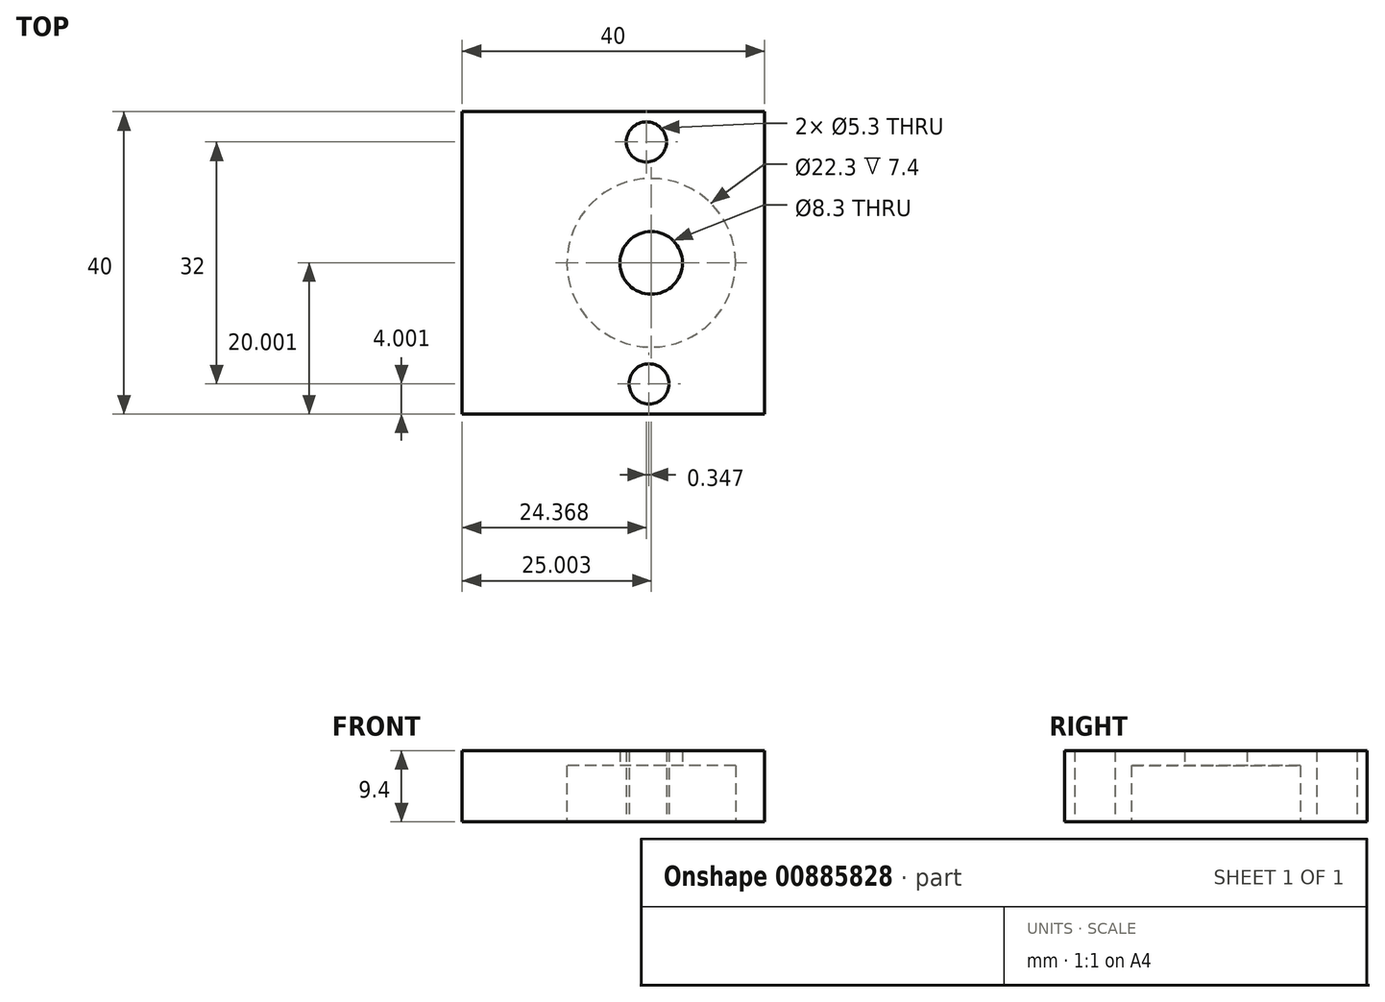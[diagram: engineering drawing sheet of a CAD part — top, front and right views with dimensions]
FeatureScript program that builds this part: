
annotation { "Feature Type Name" : "Feature", "Feature Type Description" : "" }
export const myFeature = defineFeature(function(context is Context, id is Id, definition is map)
    precondition{}
    {
        {
            var Q0;
            Q0=qCreatedBy(makeId("Top.planeOp"),FACE);
            var sketch = newSketch(context, id + "F0", { "sketchPlane" : qUnion([Q0])});
            skLineSegment(sketch, "E0.bottom", {"start": v(-86.26, -17.28) * mm, "end": v(-66.26, -17.28) * mm});
            skLineSegment(sketch, "E0.top", {"start": v(-86.26, -57.28) * mm, "end": v(-66.26, -57.28) * mm});
            skLineSegment(sketch, "E0.left", {"start": v(-86.26, -17.28) * mm, "end": v(-86.26, -57.28) * mm});
            skLineSegment(sketch, "E0.right", {"start": v(-66.26, -17.28) * mm, "end": v(-66.26, -57.28) * mm});
            skCircle(sketch, "E1", {"center": v(-76.26, -24.28) * mm, "radius": 2.65 * mm});
            skCircle(sketch, "E2", {"center": v(-76.26, -37.28) * mm, "radius": 2.65 * mm});
            skCircle(sketch, "E3", {"center": v(-76.26, -50.28) * mm, "radius": 2.65 * mm});
            skPoint(sketch, "E4", {"position": v(-66.26, -17.28) * mm});
            skPoint(sketch, "E5", {"position": v(-66.26, -57.28) * mm});
            skLineSegment(sketch, "E6.bottom", {"start": v(-66.26, -17.28) * mm, "end": v(-26.26, -17.28) * mm});
            skLineSegment(sketch, "E6.top", {"start": v(-66.26, -57.28) * mm, "end": v(-26.26, -57.28) * mm});
            skLineSegment(sketch, "E6.right", {"start": v(-26.26, -17.28) * mm, "end": v(-26.26, -57.28) * mm});
            skCircle(sketch, "E7", {"center": v(-41.26, -37.28) * mm, "radius": 4.15 * mm});
            skCircle(sketch, "E8", {"center": v(-41.26, -37.28) * mm, "radius": 11.15 * mm});
            skCircle(sketch, "E9", {"center": v(-41.9, -21.28) * mm, "radius": 2.65 * mm});
            skCircle(sketch, "E10", {"center": v(-41.54, -53.28) * mm, "radius": 2.65 * mm});
            skSolve(sketch);
        }
        {
            var Q0;
            Q0=makeQuery(id+"F0.imprint","IMPRINT",FACE,{"disambiguationData":[TD([[makeQuery(id+"F0.imprint","IMPRINT",EDGE,{"derivedFrom":sQuery(id+"F0.wireOp",EDGE,"E6.bottom")}),-1.0]])]});
            extrude(context, id + "F1", {"entities" : qUnion([Q0]), "depth" : 7.4 * mm});
        }
        {
            var Q0;
            Q0=makeQuery(id+"F1.opExtrude","CAP_FACE",FACE,{"disambiguationData":[OSD([sQuery(id+"F0.wireOp",EDGE,"E6.bottom"),sQuery(id+"F0.wireOp",EDGE,"E6.top"),sQuery(id+"F0.wireOp",EDGE,"E0.right"),sQuery(id+"F0.wireOp",EDGE,"E6.right"),sQuery(id+"F0.wireOp",EDGE,"E8"),sQuery(id+"F0.wireOp",EDGE,"E9"),sQuery(id+"F0.wireOp",EDGE,"E10")])],"isStart":false});
            var sketch = newSketch(context, id + "F2", { "sketchPlane" : qUnion([Q0])});
            skLineSegment(sketch, "E11.bottom", {"start": v(-66.26, -17.28) * mm, "end": v(-26.26, -17.28) * mm});
            skLineSegment(sketch, "E11.top", {"start": v(-66.26, -57.28) * mm, "end": v(-26.26, -57.28) * mm});
            skLineSegment(sketch, "E11.left", {"start": v(-66.26, -17.28) * mm, "end": v(-66.26, -57.28) * mm});
            skLineSegment(sketch, "E11.right", {"start": v(-26.26, -17.28) * mm, "end": v(-26.26, -57.28) * mm});
            skSolve(sketch);
        }
        {
            var Q0;
            Q0=makeQuery(id+"F2.imprint","IMPRINT",FACE,{"disambiguationData":[TD([[makeQuery(id+"F2.imprint","IMPRINT",EDGE,{"derivedFrom":sQuery(id+"F2.wireOp",EDGE,"E11.bottom")}),-1.0]])]});
            var sketch = newSketch(context, id + "F3", { "sketchPlane" : qUnion([Q0])});
            skLineSegment(sketch, "E12.bottom", {"start": v(-66.26, -17.28) * mm, "end": v(-26.26, -17.28) * mm});
            skLineSegment(sketch, "E12.top", {"start": v(-66.26, -57.28) * mm, "end": v(-26.26, -57.28) * mm});
            skLineSegment(sketch, "E12.left", {"start": v(-66.26, -17.28) * mm, "end": v(-66.26, -57.28) * mm});
            skLineSegment(sketch, "E12.right", {"start": v(-26.26, -17.28) * mm, "end": v(-26.26, -57.28) * mm});
            skPoint(sketch, "E13", {"position": v(-26.26, -17.28) * mm});
            skSolve(sketch);
        }
        {
            var Q0;
            Q0=qSketchRegion(id+"F3",true);
            var Q1;
            Q1=makeQuery(id+"F2.imprint","IMPRINT",FACE,{"disambiguationData":[TD([[makeQuery(id+"F2.imprint","IMPRINT",EDGE,{"derivedFrom":sQuery(id+"F2.wireOp",EDGE,"E11.bottom")}),-1.0]])]});
            extrude(context, id + "F4", {"entities" : qUnion([Q0, Q1]), "operationType" : NewBodyOperationType.ADD, "depth" : 2 * mm});
        }
        {
            var Q0;
            Q0=makeQuery(id+"F4.boolean.opBoolean","MERGE",FACE,{"disambiguationData":[OD(1.0)],"derivedFrom":[makeQuery(id+"F4.opExtrude","CAP_FACE",FACE,{"disambiguationData":[OSD([sQuery(id+"F0.wireOp",EDGE,"E8"),sQuery(id+"F0.wireOp",EDGE,"E9"),sQuery(id+"F0.wireOp",EDGE,"E10"),sQuery(id+"F2.wireOp",EDGE,"E11.bottom"),sQuery(id+"F2.wireOp",EDGE,"E11.top"),sQuery(id+"F2.wireOp",EDGE,"E11.left"),sQuery(id+"F2.wireOp",EDGE,"E11.right")])],"isStart":true}),makeQuery(id+"F4.opExtrude","CAP_FACE",FACE,{"disambiguationData":[OSD([sQuery(id+"F3.wireOp",EDGE,"E12.bottom"),sQuery(id+"F3.wireOp",EDGE,"E12.top"),sQuery(id+"F3.wireOp",EDGE,"E12.left"),sQuery(id+"F3.wireOp",EDGE,"E12.right")])],"isStart":true})]});
            var Q1;
            Q1=makeQuery(id+"F4.boolean.opBoolean","MERGE",FACE,{"disambiguationData":[OD(2.0)],"derivedFrom":[makeQuery(id+"F4.opExtrude","CAP_FACE",FACE,{"disambiguationData":[OSD([sQuery(id+"F0.wireOp",EDGE,"E8"),sQuery(id+"F0.wireOp",EDGE,"E9"),sQuery(id+"F0.wireOp",EDGE,"E10"),sQuery(id+"F2.wireOp",EDGE,"E11.bottom"),sQuery(id+"F2.wireOp",EDGE,"E11.top"),sQuery(id+"F2.wireOp",EDGE,"E11.left"),sQuery(id+"F2.wireOp",EDGE,"E11.right")])],"isStart":true}),makeQuery(id+"F4.opExtrude","CAP_FACE",FACE,{"disambiguationData":[OSD([sQuery(id+"F3.wireOp",EDGE,"E12.bottom"),sQuery(id+"F3.wireOp",EDGE,"E12.top"),sQuery(id+"F3.wireOp",EDGE,"E12.left"),sQuery(id+"F3.wireOp",EDGE,"E12.right")])],"isStart":true})]});
            var Q2;
            Q2=makeQuery(id+"F0.imprint","IMPRINT",FACE,{"disambiguationData":[TD([[makeQuery(id+"F0.imprint","IMPRINT",EDGE,{"derivedFrom":sQuery(id+"F0.wireOp",EDGE,"E7")}),1.0]])]});
            extrude(context, id + "F5", {"entities" : qUnion([Q0, Q1, Q2]), "operationType" : NewBodyOperationType.REMOVE, "oppositeDirection" : true, "depth" : 25 * mm});
        }
    });
